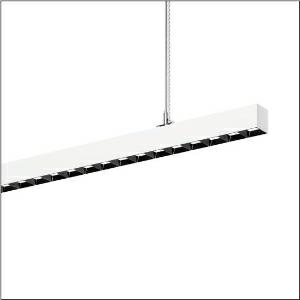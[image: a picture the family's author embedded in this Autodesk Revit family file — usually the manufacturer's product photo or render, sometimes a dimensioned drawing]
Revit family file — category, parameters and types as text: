
# Revit family: silica_r__21_51mx34dc4dwb_1888
name_source: partatom
category: Lighting Fixtures
units: mm (PartAtom-declared; Revit-internal decimal feet)

## family parameters
Cut with Voids When Loaded = No
Host = Face
Light Source = No
Part Type = Normal
Room Calculation Point = No
Round Connector Dimension = Use Diameter
Shared = No

## types (1)
- --- (1 x LED, 19200 lm, 120.3 W, 4000K)
    Apparent Load = 120 VA
    CIE Flux Codes = 74 94 99 56 100
    Color Rendering = 80
    Color Temperature = 4000K
    Default Elevation = 1800 mm
    Description = Silica® 21, office luminaire, primary light control with darklight reflector, of PMMA, black, light emission: direct/indirect distribution, primary light characteristic: asymmetric, installation type: suspended mounting, LED, rated luminous flux: 19.200lm, luminous efficacy: 160lm/W, light colour: 840, colour temperature: 4000K, with terminal, 3+2-pole, max. 2.5mm², mains connection: 220..240V, AC, 50/60Hz, rated input power: 120.3W, luminaire housing, of aluminium, traffic white (RAL 9016), length: 3.004mm, width: 53mm, height: 53mm, protection rating (complete): IP20, insulation class (complete): insulation class I (protective earthing), certification: CE, permissible operating ambient temperature: 0..+35°C, standard: EN 50419, packaging unit: 1 piece
    Height = 53 mm
    Lamp = 1 x LED
    Lamp Light Flux = 19200 lm
    Lamp Power = 120.3 W
    Lamp count = 1
    Length = 3004 mm
    Luminous efficacy = 160 lm/W
    Manufacturer = Siteco
    ModVariant = No
    Model = 51MX34DC4DWB
    Mounting Place = Ceiling
    Mounting Type = Pendant
    Number of Poles = 1
    OnlyDefault = Yes
    Power Factor = 1
    Product Name = Silica® 21
    Product group = office luminaire | ceiling pendant
    ProductGroupID = 905
    Protection Class = Protection class I
    Protection Degree = IP 20
    RLX_Detail_Level = 1
    RlxData = <blob elided: 66745 chars, md5=10917811>
    Socket = socket
    Standby Power = 0 W
    System Light Flux = 19200 lm
    System Power = 120 W
    Type Comments = factory setting: luminous flux: 100 % | dim-lin: 254 | 418 mA
    Type Image = l_1251637.jpg
    URL = http://relux.com
    VarID = @adj_029363
    Voltage = 0 V
    Weight = 0.00 kg
    Width = 53 mm

## geometry (parser evidence)
native form markers: Blend x4, Sweep x14
no freeform markers — native parametric forms only
